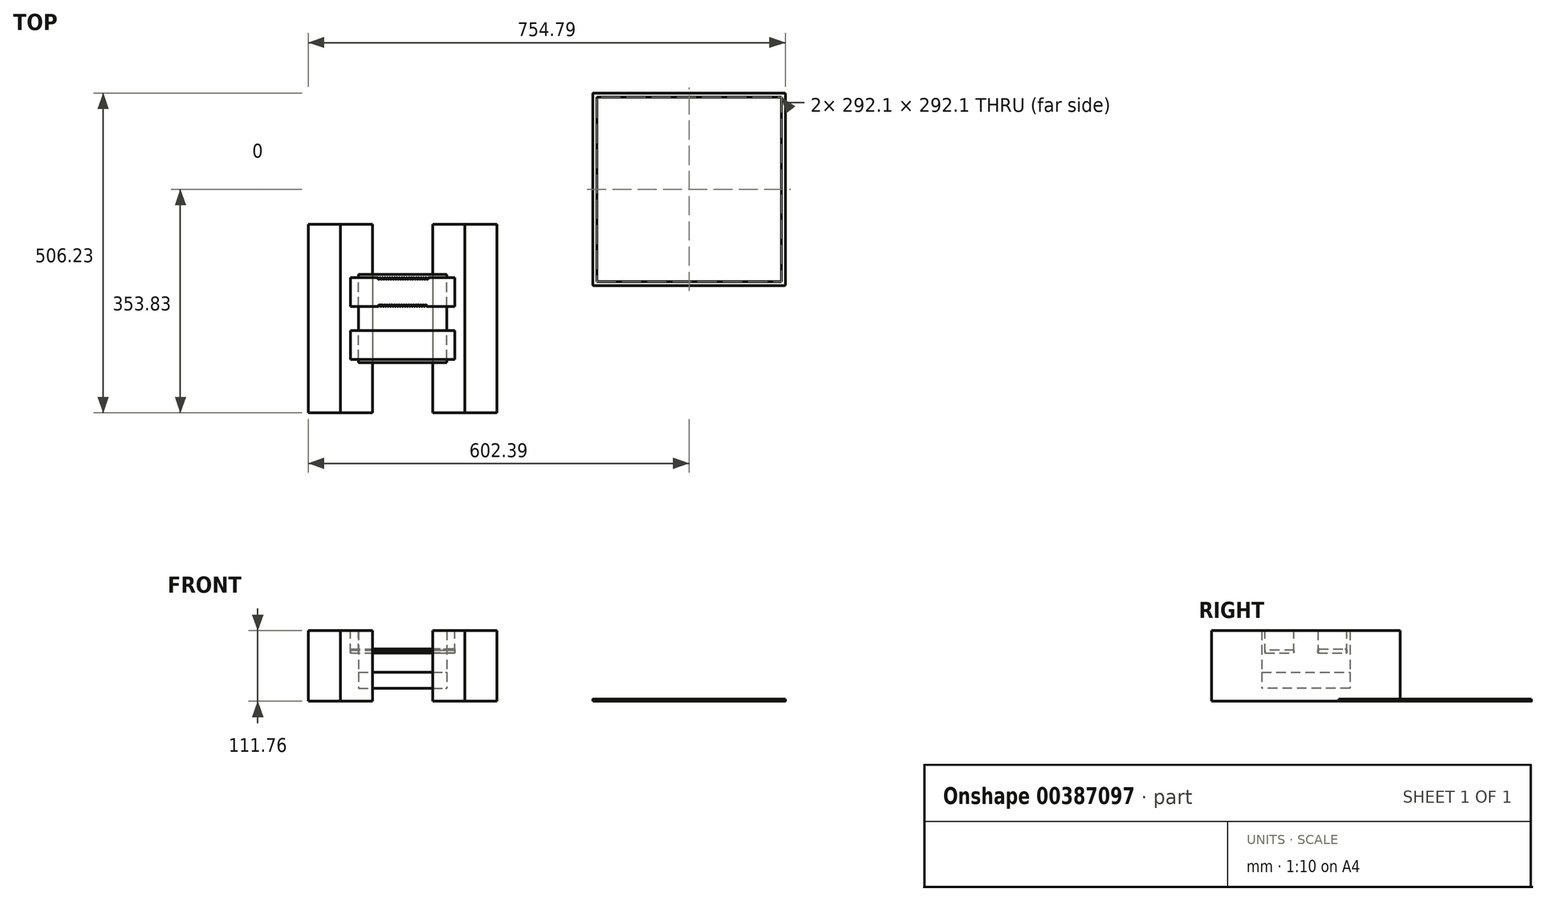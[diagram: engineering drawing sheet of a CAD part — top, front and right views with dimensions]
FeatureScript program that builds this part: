
annotation { "Feature Type Name" : "Feature", "Feature Type Description" : "" }
export const myFeature = defineFeature(function(context is Context, id is Id, definition is map)
    precondition{}
    {
        {
            var Q0;
            Q0=qCreatedBy(makeId("Top.planeOp"),FACE);
            var sketch = newSketch(context, id + "F0", { "sketchPlane" : qUnion([Q0])});
            skLineSegment(sketch, "E0.bottom", {"start": v(0, 0) * mm, "end": v(304.8, 0) * mm});
            skLineSegment(sketch, "E0.top", {"start": v(0, 304.8) * mm, "end": v(304.8, 304.8) * mm});
            skLineSegment(sketch, "E0.left", {"start": v(0, 0) * mm, "end": v(0, 304.8) * mm});
            skLineSegment(sketch, "E0.right", {"start": v(304.8, 0) * mm, "end": v(304.8, 304.8) * mm});
            skLineSegment(sketch, "E1.bottom", {"start": v(6.35, 6.35) * mm, "end": v(298.45, 6.35) * mm});
            skLineSegment(sketch, "E1.top", {"start": v(6.35, 298.45) * mm, "end": v(298.45, 298.45) * mm});
            skLineSegment(sketch, "E1.left", {"start": v(6.35, 6.35) * mm, "end": v(6.35, 298.45) * mm});
            skLineSegment(sketch, "E1.right", {"start": v(298.45, 6.35) * mm, "end": v(298.45, 298.45) * mm});
            skLineSegment(sketch, "E2.bottom", {"start": v(0, -50.8) * mm, "end": v(111.63, -50.8) * mm});
            skLineSegment(sketch, "E2.top", {"start": v(0, -349.12) * mm, "end": v(111.63, -349.12) * mm});
            skLineSegment(sketch, "E2.left", {"start": v(0, -50.8) * mm, "end": v(0, -349.12) * mm});
            skLineSegment(sketch, "E2.right", {"start": v(111.63, -50.8) * mm, "end": v(111.63, -349.12) * mm});
            skPoint(sketch, "E3", {"position": v(0, -50.8) * mm});
            skLineSegment(sketch, "E4.bottom", {"start": v(177.3, -349.12) * mm, "end": v(288.93, -349.12) * mm});
            skLineSegment(sketch, "E4.top", {"start": v(177.3, -50.94) * mm, "end": v(288.93, -50.94) * mm});
            skLineSegment(sketch, "E4.left", {"start": v(177.3, -349.12) * mm, "end": v(177.3, -50.94) * mm});
            skLineSegment(sketch, "E4.right", {"start": v(288.93, -349.12) * mm, "end": v(288.93, -50.94) * mm});
            skLineSegment(sketch, "E5.bottom", {"start": v(-449.99, 97.02) * mm, "end": v(-151.54, 97.02) * mm});
            skLineSegment(sketch, "E5.top", {"start": v(-449.99, -201.43) * mm, "end": v(-151.54, -201.43) * mm});
            skLineSegment(sketch, "E5.left", {"start": v(-449.99, 97.02) * mm, "end": v(-449.99, -201.43) * mm});
            skLineSegment(sketch, "E5.right", {"start": v(-151.54, 97.02) * mm, "end": v(-151.54, -201.43) * mm});
            skPoint(sketch, "E6", {"position": v(-399.19, 97.02) * mm});
            skPoint(sketch, "E7", {"position": v(-202.34, 97.02) * mm});
            skPoint(sketch, "E8", {"position": v(-348.39, 97.02) * mm});
            skPoint(sketch, "E9", {"position": v(-253.14, 97.02) * mm});
            skLineSegment(sketch, "E10", {"start": v(-399.19, 97.02) * mm, "end": v(-399.19, -201.43) * mm});
            skLineSegment(sketch, "E11", {"start": v(-348.39, 97.02) * mm, "end": v(-348.39, -201.43) * mm});
            skLineSegment(sketch, "E12", {"start": v(-253.14, 97.02) * mm, "end": v(-253.14, -201.43) * mm});
            skLineSegment(sketch, "E13", {"start": v(-202.34, 97.02) * mm, "end": v(-202.34, -201.43) * mm});
            skPoint(sketch, "E14", {"position": v(-253.14, -52.2) * mm});
            skLineSegment(sketch, "E15", {"start": v(-253.14, -52.2) * mm, "end": v(-348.39, -52.2) * mm, "construction": true});
            skPoint(sketch, "E16", {"position": v(-300.76, -52.2) * mm});
            skLineSegment(sketch, "E17.bottom", {"start": v(-370.61, -122.06) * mm, "end": v(-230.91, -122.06) * mm});
            skLineSegment(sketch, "E17.top", {"start": v(-370.61, 17.64) * mm, "end": v(-230.91, 17.64) * mm});
            skLineSegment(sketch, "E17.left", {"start": v(-370.61, -122.06) * mm, "end": v(-370.61, 17.64) * mm});
            skLineSegment(sketch, "E17.right", {"start": v(-230.91, -122.06) * mm, "end": v(-230.91, 17.64) * mm});
            skSolve(sketch);
        }
        {
            var Q0;
            Q0=makeQuery(id+"F0.imprint","IMPRINT",FACE,{"disambiguationData":[TD([[makeQuery(id+"F0.imprint","IMPRINT",EDGE,{"derivedFrom":sQuery(id+"F0.wireOp",EDGE,"E0.bottom")}),1.0]])]});
            extrude(context, id + "F1", {"entities" : qUnion([Q0]), "depth" : 3.17 * mm});
        }
        {
            var Q0;
            Q0=makeQuery(id+"F1.opExtrude","SWEPT_EDGE",EDGE,{"disambiguationData":[OSD([sQuery(id+"F0.wireOp",EDGE,"E0.bottom"),sQuery(id+"F0.wireOp",EDGE,"E0.left")])]});
            var Q1;
            Q1=makeQuery(id+"F1.opExtrude","SWEPT_EDGE",EDGE,{"disambiguationData":[OSD([sQuery(id+"F0.wireOp",EDGE,"E0.bottom"),sQuery(id+"F0.wireOp",EDGE,"E0.right")])]});
            var Q2;
            Q2=makeQuery(id+"F1.opExtrude","SWEPT_EDGE",EDGE,{"disambiguationData":[OSD([sQuery(id+"F0.wireOp",EDGE,"E0.top"),sQuery(id+"F0.wireOp",EDGE,"E0.right")])]});
            var Q3;
            Q3=makeQuery(id+"F1.opExtrude","SWEPT_EDGE",EDGE,{"disambiguationData":[OSD([sQuery(id+"F0.wireOp",EDGE,"E0.top"),sQuery(id+"F0.wireOp",EDGE,"E0.left")])]});
            fillet(context, id + "F2", {"entities" : qUnion([Q0, Q1, Q2, Q3]), "radius" : 1.27 * mm, "tangentPropagation" : true, "allowEdgeOverflow" : false});
        }
        {
            var Q0;
            {var subQ5=sQuery(id+"F0.wireOp",EDGE,"E10");Q0=makeQuery(id+"F0.imprint","IMPRINT",FACE,{"disambiguationData":[TD([[makeQuery(id+"F0.imprint","IMPRINT",EDGE,{"derivedFrom":subQ5}),1.0]])]});}
            var Q1;
            {var subQ10=sQuery(id+"F0.wireOp",EDGE,"E13");Q1=makeQuery(id+"F0.imprint","IMPRINT",FACE,{"disambiguationData":[TD([[makeQuery(id+"F0.imprint","IMPRINT",EDGE,{"derivedFrom":subQ10}),-1.0]])]});}
            extrude(context, id + "F3", {"entities" : qUnion([Q0, Q1]), "operationType" : NewBodyOperationType.ADD, "depth" : 111.76 * mm});
        }
        {
            var Q0;
            {var subQ5=sQuery(id+"F0.wireOp",EDGE,"E17.left");Q0=makeQuery(id+"F0.imprint","IMPRINT",FACE,{"disambiguationData":[TD([[makeQuery(id+"F0.imprint","IMPRINT",EDGE,{"derivedFrom":subQ5}),-1.0]])]});}
            var Q1;
            {var subQ5=sQuery(id+"F0.wireOp",EDGE,"E17.right");Q1=makeQuery(id+"F0.imprint","IMPRINT",FACE,{"disambiguationData":[TD([[makeQuery(id+"F0.imprint","IMPRINT",EDGE,{"derivedFrom":subQ5}),1.0]])]});}
            extrude(context, id + "F4", {"entities" : qUnion([Q0, Q1]), "operationType" : NewBodyOperationType.ADD, "depth" : 20.32 * mm});
        }
        {
            var Q0;
            Q0=makeQuery(id+"F3.opExtrude","CAP_FACE",FACE,{"disambiguationData":[OSD([sQuery(id+"F0.wireOp",EDGE,"E5.bottom"),sQuery(id+"F0.wireOp",EDGE,"E5.top"),sQuery(id+"F0.wireOp",EDGE,"E5.left"),sQuery(id+"F0.wireOp",EDGE,"E11"),sQuery(id+"F0.wireOp",EDGE,"E17.bottom"),sQuery(id+"F0.wireOp",EDGE,"E17.top"),sQuery(id+"F0.wireOp",EDGE,"E17.left")])],"isStart":false});
            var Q1;
            Q1=makeQuery(id+"F3.opExtrude","CAP_FACE",FACE,{"disambiguationData":[OSD([sQuery(id+"F0.wireOp",EDGE,"E5.bottom"),sQuery(id+"F0.wireOp",EDGE,"E5.top"),sQuery(id+"F0.wireOp",EDGE,"E5.right"),sQuery(id+"F0.wireOp",EDGE,"E12"),sQuery(id+"F0.wireOp",EDGE,"E17.bottom"),sQuery(id+"F0.wireOp",EDGE,"E17.top"),sQuery(id+"F0.wireOp",EDGE,"E17.right")])],"isStart":false});
            cPlane(context, id + "F5", {"entities" : qUnion([Q0, Q1]), "cplaneType" : CPlaneType.MID_PLANE, "offset" : 25.4 * mm, "width" : 152.4 * mm, "height" : 152.4 * mm});
        }
        {
            var Q0;
            Q0=qCreatedBy(id+"F5.planeOp",FACE);
            var sketch = newSketch(context, id + "F6", { "sketchPlane" : qUnion([Q0])});
            skLineSegment(sketch, "E18.left", {"start": v(-383.31, -33.16) * mm, "end": v(-383.31, 12.56) * mm});
            skLineSegment(sketch, "E18.right", {"start": v(-218.21, -33.16) * mm, "end": v(-218.21, 12.56) * mm});
            skPoint(sketch, "E19", {"position": v(-300.76, -33.16) * mm});
            skLineSegment(sketch, "E20.MirrorCS", {"start": v(-383.31, -71.26) * mm, "end": v(-218.21, -71.26) * mm});
            skLineSegment(sketch, "E21.MirrorCS", {"start": v(-383.31, -116.98) * mm, "end": v(-218.21, -116.98) * mm});
            skLineSegment(sketch, "E22.MirrorCS", {"start": v(-218.21, -71.26) * mm, "end": v(-218.21, -116.98) * mm});
            skLineSegment(sketch, "E23.MirrorCS", {"start": v(-383.31, -71.26) * mm, "end": v(-383.31, -116.98) * mm});
            skPoint(sketch, "E24", {"position": v(-338.23, 11.3) * mm});
            skPoint(sketch, "E25.1.0.0", {"position": v(-334.42, 11.3) * mm});
            skPoint(sketch, "E25.2.0.0", {"position": v(-330.6, 11.3) * mm});
            skPoint(sketch, "E25.3.0.0", {"position": v(-326.8, 11.3) * mm});
            skPoint(sketch, "E25.4.0.0", {"position": v(-322.99, 11.3) * mm});
            skPoint(sketch, "E25.5.0.0", {"position": v(-319.18, 11.3) * mm});
            skPoint(sketch, "E25.6.0.0", {"position": v(-315.37, 11.3) * mm});
            skPoint(sketch, "E25.7.0.0", {"position": v(-311.56, 11.3) * mm});
            skPoint(sketch, "E25.8.0.0", {"position": v(-307.75, 11.3) * mm});
            skPoint(sketch, "E25.9.0.0", {"position": v(-303.94, 11.3) * mm});
            skPoint(sketch, "E25.10.0.0", {"position": v(-300.13, 11.3) * mm});
            skPoint(sketch, "E25.11.0.0", {"position": v(-296.32, 11.3) * mm});
            skPoint(sketch, "E25.12.0.0", {"position": v(-292.5, 11.3) * mm});
            skPoint(sketch, "E25.13.0.0", {"position": v(-288.7, 11.3) * mm});
            skPoint(sketch, "E25.14.0.0", {"position": v(-284.89, 11.3) * mm});
            skPoint(sketch, "E25.15.0.0", {"position": v(-281.08, 11.3) * mm});
            skPoint(sketch, "E25.16.0.0", {"position": v(-277.27, 11.3) * mm});
            skPoint(sketch, "E25.17.0.0", {"position": v(-273.46, 11.3) * mm});
            skPoint(sketch, "E25.18.0.0", {"position": v(-269.65, 11.3) * mm});
            skPoint(sketch, "E25.19.0.0", {"position": v(-265.84, 11.3) * mm});
            skPoint(sketch, "E25.20.0.0", {"position": v(-262.03, 11.3) * mm});
            skLineSegment(sketch, "E25.direction1", {"start": v(-338.23, 11.3) * mm, "end": v(-334.42, 11.3) * mm, "construction": true});
            skPoint(sketch, "E26", {"position": v(-336.96, -31.89) * mm});
            skPoint(sketch, "E27.1.0.0", {"position": v(-333.15, -31.89) * mm});
            skPoint(sketch, "E27.2.0.0", {"position": v(-329.34, -31.89) * mm});
            skPoint(sketch, "E27.3.0.0", {"position": v(-325.53, -31.89) * mm});
            skPoint(sketch, "E27.4.0.0", {"position": v(-321.72, -31.89) * mm});
            skPoint(sketch, "E27.5.0.0", {"position": v(-317.9, -31.89) * mm});
            skPoint(sketch, "E27.6.0.0", {"position": v(-314.1, -31.89) * mm});
            skPoint(sketch, "E27.7.0.0", {"position": v(-310.29, -31.89) * mm});
            skPoint(sketch, "E27.8.0.0", {"position": v(-306.48, -31.89) * mm});
            skPoint(sketch, "E27.9.0.0", {"position": v(-302.67, -31.89) * mm});
            skPoint(sketch, "E27.10.0.0", {"position": v(-298.86, -31.89) * mm});
            skPoint(sketch, "E27.11.0.0", {"position": v(-295.05, -31.89) * mm});
            skPoint(sketch, "E27.12.0.0", {"position": v(-291.24, -31.89) * mm});
            skPoint(sketch, "E27.13.0.0", {"position": v(-287.43, -31.89) * mm});
            skPoint(sketch, "E27.14.0.0", {"position": v(-283.62, -31.89) * mm});
            skPoint(sketch, "E27.15.0.0", {"position": v(-279.8, -31.89) * mm});
            skPoint(sketch, "E27.16.0.0", {"position": v(-276, -31.89) * mm});
            skPoint(sketch, "E27.17.0.0", {"position": v(-272.19, -31.89) * mm});
            skPoint(sketch, "E27.18.0.0", {"position": v(-268.38, -31.89) * mm});
            skPoint(sketch, "E27.19.0.0", {"position": v(-264.57, -31.89) * mm});
            skLineSegment(sketch, "E27.direction1", {"start": v(-336.96, -31.89) * mm, "end": v(-333.15, -31.89) * mm, "construction": true});
            skPoint(sketch, "E28", {"position": v(-340.13, 12.56) * mm});
            skPoint(sketch, "E29.1.0.0", {"position": v(472.67, 12.56) * mm});
            skPoint(sketch, "E29.2.0.0", {"position": v(1285.47, 12.56) * mm});
            skLineSegment(sketch, "E29.direction1", {"start": v(-340.13, 12.56) * mm, "end": v(472.67, 12.56) * mm, "construction": true});
            skPoint(sketch, "E30.1.0.0", {"position": v(-336.32, 12.56) * mm});
            skPoint(sketch, "E30.2.0.0", {"position": v(-332.51, 12.56) * mm});
            skPoint(sketch, "E30.3.0.0", {"position": v(-328.7, 12.56) * mm});
            skPoint(sketch, "E30.4.0.0", {"position": v(-324.9, 12.56) * mm});
            skPoint(sketch, "E30.5.0.0", {"position": v(-321.08, 12.56) * mm});
            skPoint(sketch, "E30.6.0.0", {"position": v(-317.27, 12.56) * mm});
            skPoint(sketch, "E30.7.0.0", {"position": v(-313.46, 12.56) * mm});
            skPoint(sketch, "E30.8.0.0", {"position": v(-309.65, 12.56) * mm});
            skPoint(sketch, "E30.9.0.0", {"position": v(-305.84, 12.56) * mm});
            skPoint(sketch, "E30.10.0.0", {"position": v(-302.03, 12.56) * mm});
            skPoint(sketch, "E30.11.0.0", {"position": v(-298.22, 12.56) * mm});
            skPoint(sketch, "E30.12.0.0", {"position": v(-294.41, 12.56) * mm});
            skPoint(sketch, "E30.13.0.0", {"position": v(-290.6, 12.56) * mm});
            skPoint(sketch, "E30.14.0.0", {"position": v(-286.8, 12.56) * mm});
            skPoint(sketch, "E30.15.0.0", {"position": v(-282.98, 12.56) * mm});
            skPoint(sketch, "E30.16.0.0", {"position": v(-279.17, 12.56) * mm});
            skPoint(sketch, "E30.17.0.0", {"position": v(-275.36, 12.56) * mm});
            skPoint(sketch, "E30.18.0.0", {"position": v(-271.55, 12.56) * mm});
            skPoint(sketch, "E30.19.0.0", {"position": v(-267.74, 12.56) * mm});
            skPoint(sketch, "E30.20.0.0", {"position": v(-263.93, 12.56) * mm});
            skPoint(sketch, "E30.21.0.0", {"position": v(-260.12, 12.56) * mm});
            skLineSegment(sketch, "E30.direction1", {"start": v(-340.13, 12.56) * mm, "end": v(-336.32, 12.56) * mm, "construction": true});
            skLineSegment(sketch, "E31", {"start": v(-383.31, 12.56) * mm, "end": v(-340.13, 12.56) * mm});
            skLineSegment(sketch, "E32", {"start": v(-260.12, 12.56) * mm, "end": v(-218.21, 12.56) * mm});
            skFitSpline(sketch, "E33", {"points": [v(-340.13, 12.56) * mm, v(-338.23, 11.3) * mm, v(-336.32, 12.56) * mm, v(-334.42, 11.3) * mm, v(-332.51, 12.56) * mm, v(-330.6, 11.3) * mm, v(-328.7, 12.56) * mm, v(-326.8, 11.3) * mm, v(-324.9, 12.56) * mm, v(-322.99, 11.3) * mm, v(-321.08, 12.56) * mm, v(-319.18, 11.3) * mm, v(-317.27, 12.56) * mm, v(-315.37, 11.3) * mm, v(-313.46, 12.56) * mm, v(-311.56, 11.3) * mm, v(-309.65, 12.56) * mm, v(-307.75, 11.3) * mm, v(-305.84, 12.56) * mm, v(-303.94, 11.3) * mm, v(-302.03, 12.56) * mm, v(-300.13, 11.3) * mm, v(-298.22, 12.56) * mm, v(-296.32, 11.3) * mm, v(-294.41, 12.56) * mm, v(-292.5, 11.3) * mm, v(-290.6, 12.56) * mm, v(-288.7, 11.3) * mm, v(-286.8, 12.56) * mm, v(-284.89, 11.3) * mm, v(-282.98, 12.56) * mm, v(-281.08, 11.3) * mm, v(-279.17, 12.56) * mm, v(-277.27, 11.3) * mm, v(-275.36, 12.56) * mm, v(-273.46, 11.3) * mm, v(-271.55, 12.56) * mm, v(-269.65, 11.3) * mm, v(-267.74, 12.56) * mm, v(-265.84, 11.3) * mm, v(-263.93, 12.56) * mm, v(-262.03, 11.3) * mm, v(-260.12, 12.56) * mm], "startDerivative": vector(80.01, -92.39) * mm, "endDerivative": vector(80, 92.39) * mm});
            skPoint(sketch, "E34", {"position": v(-338.86, -33.16) * mm});
            skPoint(sketch, "E35.0.22.0", {"position": v(-256.31, 12.56) * mm});
            skPoint(sketch, "E36.1.0.0", {"position": v(-335.05, -33.16) * mm});
            skPoint(sketch, "E36.2.0.0", {"position": v(-331.24, -33.16) * mm});
            skPoint(sketch, "E36.3.0.0", {"position": v(-327.43, -33.16) * mm});
            skPoint(sketch, "E36.4.0.0", {"position": v(-323.62, -33.16) * mm});
            skPoint(sketch, "E36.5.0.0", {"position": v(-319.81, -33.16) * mm});
            skPoint(sketch, "E36.6.0.0", {"position": v(-316, -33.16) * mm});
            skPoint(sketch, "E36.7.0.0", {"position": v(-312.2, -33.16) * mm});
            skPoint(sketch, "E36.8.0.0", {"position": v(-308.38, -33.16) * mm});
            skPoint(sketch, "E36.9.0.0", {"position": v(-304.57, -33.16) * mm});
            skPoint(sketch, "E36.11.0.0", {"position": v(-296.95, -33.16) * mm});
            skPoint(sketch, "E36.12.0.0", {"position": v(-293.14, -33.16) * mm});
            skPoint(sketch, "E36.13.0.0", {"position": v(-289.33, -33.16) * mm});
            skPoint(sketch, "E36.14.0.0", {"position": v(-285.52, -33.16) * mm});
            skPoint(sketch, "E36.15.0.0", {"position": v(-281.71, -33.16) * mm});
            skPoint(sketch, "E36.16.0.0", {"position": v(-277.9, -33.16) * mm});
            skPoint(sketch, "E36.17.0.0", {"position": v(-274.1, -33.16) * mm});
            skPoint(sketch, "E36.18.0.0", {"position": v(-270.28, -33.16) * mm});
            skPoint(sketch, "E36.19.0.0", {"position": v(-266.47, -33.16) * mm});
            skPoint(sketch, "E36.20.0.0", {"position": v(-262.66, -33.16) * mm});
            skPoint(sketch, "E36.21.0.0", {"position": v(-258.85, -33.16) * mm});
            skLineSegment(sketch, "E36.direction1", {"start": v(-338.86, -33.16) * mm, "end": v(-335.05, -33.16) * mm, "construction": true});
            skFitSpline(sketch, "E37", {"points": [v(-338.86, -33.16) * mm, v(-336.96, -31.89) * mm, v(-335.05, -33.16) * mm, v(-333.15, -31.89) * mm, v(-331.24, -33.16) * mm, v(-329.34, -31.89) * mm, v(-327.43, -33.16) * mm, v(-325.53, -31.89) * mm, v(-323.62, -33.16) * mm, v(-321.72, -31.89) * mm, v(-319.81, -33.16) * mm, v(-317.9, -31.89) * mm, v(-316, -33.16) * mm, v(-314.1, -31.89) * mm, v(-312.2, -33.16) * mm, v(-310.29, -31.89) * mm, v(-308.38, -33.16) * mm, v(-306.48, -31.89) * mm, v(-304.57, -33.16) * mm, v(-302.67, -31.89) * mm, v(-300.76, -33.16) * mm, v(-298.86, -31.89) * mm, v(-296.95, -33.16) * mm, v(-295.05, -31.89) * mm, v(-293.14, -33.16) * mm, v(-291.24, -31.89) * mm, v(-289.33, -33.16) * mm, v(-287.43, -31.89) * mm, v(-285.52, -33.16) * mm, v(-283.62, -31.89) * mm, v(-281.71, -33.16) * mm, v(-279.8, -31.89) * mm, v(-277.9, -33.16) * mm, v(-276, -31.89) * mm, v(-274.1, -33.16) * mm, v(-272.19, -31.89) * mm, v(-270.28, -33.16) * mm, v(-268.38, -31.89) * mm, v(-266.47, -33.16) * mm, v(-264.57, -31.89) * mm, v(-262.66, -33.16) * mm], "startDerivative": vector(76.2, 87.99) * mm, "endDerivative": vector(76.2, -87.99) * mm});
            skLineSegment(sketch, "E38", {"start": v(-383.31, -33.16) * mm, "end": v(-338.86, -33.16) * mm});
            skLineSegment(sketch, "E39", {"start": v(-218.21, -33.16) * mm, "end": v(-262.66, -33.16) * mm});
            skSolve(sketch);
        }
        {
            var Q0;
            Q0=makeQuery(id+"F6.imprint","IMPRINT",FACE,{"disambiguationData":[TD([[makeQuery(id+"F6.imprint","IMPRINT",EDGE,{"derivedFrom":sQuery(id+"F6.wireOp",EDGE,"E18.left")}),-1.0]])]});
            var Q1;
            Q1=makeQuery(id+"F6.imprint","IMPRINT",FACE,{"disambiguationData":[TD([[makeQuery(id+"F6.imprint","IMPRINT",EDGE,{"derivedFrom":sQuery(id+"F6.wireOp",EDGE,"E20.MirrorCS")}),-1.0]])]});
            extrude(context, id + "F7", {"entities" : qUnion([Q0, Q1]), "operationType" : NewBodyOperationType.REMOVE, "oppositeDirection" : true, "depth" : 35.56 * mm});
        }
        {
            var Q0;
            {var subQ0=sQuery(id+"F0.wireOp",EDGE,"E5.left");Q0=makeQuery(id+"F0.imprint","IMPRINT",FACE,{"disambiguationData":[TD([[makeQuery(id+"F0.imprint","IMPRINT",EDGE,{"derivedFrom":subQ0}),1.0]])]});}
            var Q1;
            {var subQ0=sQuery(id+"F0.wireOp",EDGE,"E5.right");Q1=makeQuery(id+"F0.imprint","IMPRINT",FACE,{"disambiguationData":[TD([[makeQuery(id+"F0.imprint","IMPRINT",EDGE,{"derivedFrom":subQ0}),-1.0]])]});}
            extrude(context, id + "F8", {"entities" : qUnion([Q0, Q1]), "depth" : 111.76 * mm});
        }
        {
            var Q0;
            Q0=makeQuery(id+"F6.imprint","IMPRINT",FACE,{"disambiguationData":[TD([[makeQuery(id+"F6.imprint","IMPRINT",EDGE,{"derivedFrom":sQuery(id+"F6.wireOp",EDGE,"E20.MirrorCS")}),-1.0]])]});
            extrude(context, id + "F9", {"entities" : qUnion([Q0]), "depth" : 4.76 * mm});
        }
        {
            var Q0;
            {var subQ0=sQuery(id+"F0.wireOp",EDGE,"E17.top");var subQ1=sQuery(id+"F0.wireOp",EDGE,"E11");var subQ2=makeQuery(id+"F0.imprint","INTERSECT",VERTEX,{"derivedFrom":[subQ1,subQ0]});Q0=makeQuery(id+"F0.imprint","IMPRINT",FACE,{"disambiguationData":[TD([[makeQuery(id+"F0.imprint","IMPRINT",EDGE,{"disambiguationData":[TD([[subQ2,-1.0]])],"derivedFrom":subQ1}),1.0]])]});}
            var Q1;
            {var subQ5=sQuery(id+"F0.wireOp",EDGE,"E17.left");Q1=makeQuery(id+"F0.imprint","IMPRINT",FACE,{"disambiguationData":[TD([[makeQuery(id+"F0.imprint","IMPRINT",EDGE,{"derivedFrom":subQ5}),-1.0]])]});}
            var Q2;
            {var subQ5=sQuery(id+"F0.wireOp",EDGE,"E17.right");Q2=makeQuery(id+"F0.imprint","IMPRINT",FACE,{"disambiguationData":[TD([[makeQuery(id+"F0.imprint","IMPRINT",EDGE,{"derivedFrom":subQ5}),1.0]])]});}
            var Q3;
            Q3=sQuery(id+"F0.wireOp",EDGE,"E17.left");
            var Q4;
            Q4=sQuery(id+"F0.wireOp",EDGE,"E17.top");
            var Q5;
            Q5=sQuery(id+"F0.wireOp",EDGE,"E17.right");
            var Q6;
            Q6=sQuery(id+"F0.wireOp",EDGE,"E17.bottom");
            extrude(context, id + "F10", {"entities" : qUnion([Q0, Q1, Q2]), "surfaceEntities" : qUnion([Q3, Q4, Q5, Q6]), "depth" : 25.4 * mm});
        }
        {
            var Q0;
            Q0=makeQuery(id+"F10.opExtrude","SWEPT_BODY",BODY,{"disambiguationData":[OSD([sQuery(id+"F0.wireOp",EDGE,"E17.bottom"),sQuery(id+"F0.wireOp",EDGE,"E17.top"),sQuery(id+"F0.wireOp",EDGE,"E17.left"),sQuery(id+"F0.wireOp",EDGE,"E17.right")])]});
            transform(context, id + "F11", {"entities" : qUnion([Q0]), "transformType" : TransformType.TRANSLATION_3D, "dx" : 0 * mm, "dy" : 0 * mm, "dz" : 20.32 * mm, "makeCopy" : false});
        }
        {
            var Q0;
            Q0=makeQuery(id+"F6.imprint","IMPRINT",FACE,{"disambiguationData":[TD([[makeQuery(id+"F6.imprint","IMPRINT",EDGE,{"derivedFrom":sQuery(id+"F6.wireOp",EDGE,"E18.left")}),-1.0]])]});
            extrude(context, id + "F12", {"entities" : qUnion([Q0]), "depth" : 6.35 * mm});
        }
        {
            var Q0;
            Q0=makeQuery(id+"F12.opExtrude","CAP_EDGE",EDGE,{"disambiguationData":[OSD([sQuery(id+"F6.wireOp",EDGE,"E37")])],"isStart":false});
            var Q1;
            Q1=makeQuery(id+"F12.opExtrude","CAP_EDGE",EDGE,{"disambiguationData":[OSD([sQuery(id+"F6.wireOp",EDGE,"E39")])],"isStart":false});
            var Q2;
            Q2=makeQuery(id+"F12.opExtrude","CAP_EDGE",EDGE,{"disambiguationData":[OSD([sQuery(id+"F6.wireOp",EDGE,"E38")])],"isStart":false});
            var Q3;
            Q3=makeQuery(id+"F12.opExtrude","CAP_EDGE",EDGE,{"disambiguationData":[OSD([sQuery(id+"F6.wireOp",EDGE,"E33")])],"isStart":false});
            var Q4;
            Q4=makeQuery(id+"F12.opExtrude","CAP_EDGE",EDGE,{"disambiguationData":[OSD([sQuery(id+"F6.wireOp",EDGE,"E31")])],"isStart":false});
            var Q5;
            Q5=makeQuery(id+"F12.opExtrude","CAP_EDGE",EDGE,{"disambiguationData":[OSD([sQuery(id+"F6.wireOp",EDGE,"E32")])],"isStart":false});
            fillet(context, id + "F13", {"entities" : qUnion([Q0, Q1, Q2, Q3, Q4, Q5]), "radius" : 1.27 * mm, "tangentPropagation" : true, "allowEdgeOverflow" : false});
        }
        {
            var Q0;
            Q0=makeQuery(id+"F9.opExtrude","SWEPT_BODY",BODY,{"disambiguationData":[OSD([sQuery(id+"F6.wireOp",EDGE,"E20.MirrorCS"),sQuery(id+"F6.wireOp",EDGE,"E21.MirrorCS"),sQuery(id+"F6.wireOp",EDGE,"E22.MirrorCS"),sQuery(id+"F6.wireOp",EDGE,"E23.MirrorCS")])]});
            var Q1;
            Q1=makeQuery(id+"F9.opExtrude","SWEPT_BODY",BODY,{"disambiguationData":[OSD([sQuery(id+"F6.wireOp",EDGE,"E18.left"),sQuery(id+"F6.wireOp",EDGE,"E18.right"),sQuery(id+"F6.wireOp",EDGE,"E31"),sQuery(id+"F6.wireOp",EDGE,"E32"),sQuery(id+"F6.wireOp",EDGE,"E33"),sQuery(id+"F6.wireOp",EDGE,"E37"),sQuery(id+"F6.wireOp",EDGE,"E38"),sQuery(id+"F6.wireOp",EDGE,"E39")])]});
            var Q2;
            Q2=makeQuery(id+"F12.opExtrude","SWEPT_BODY",BODY,{"disambiguationData":[OSD([sQuery(id+"F6.wireOp",EDGE,"E18.left"),sQuery(id+"F6.wireOp",EDGE,"E18.right"),sQuery(id+"F6.wireOp",EDGE,"E31"),sQuery(id+"F6.wireOp",EDGE,"E32"),sQuery(id+"F6.wireOp",EDGE,"E33"),sQuery(id+"F6.wireOp",EDGE,"E37"),sQuery(id+"F6.wireOp",EDGE,"E38"),sQuery(id+"F6.wireOp",EDGE,"E39")])]});
            transform(context, id + "F14", {"entities" : qUnion([Q0, Q1, Q2]), "transformType" : TransformType.TRANSLATION_3D, "dx" : 0 * mm, "dy" : 0 * mm, "dz" : -35.56 * mm, "makeCopy" : false});
        }
    });
